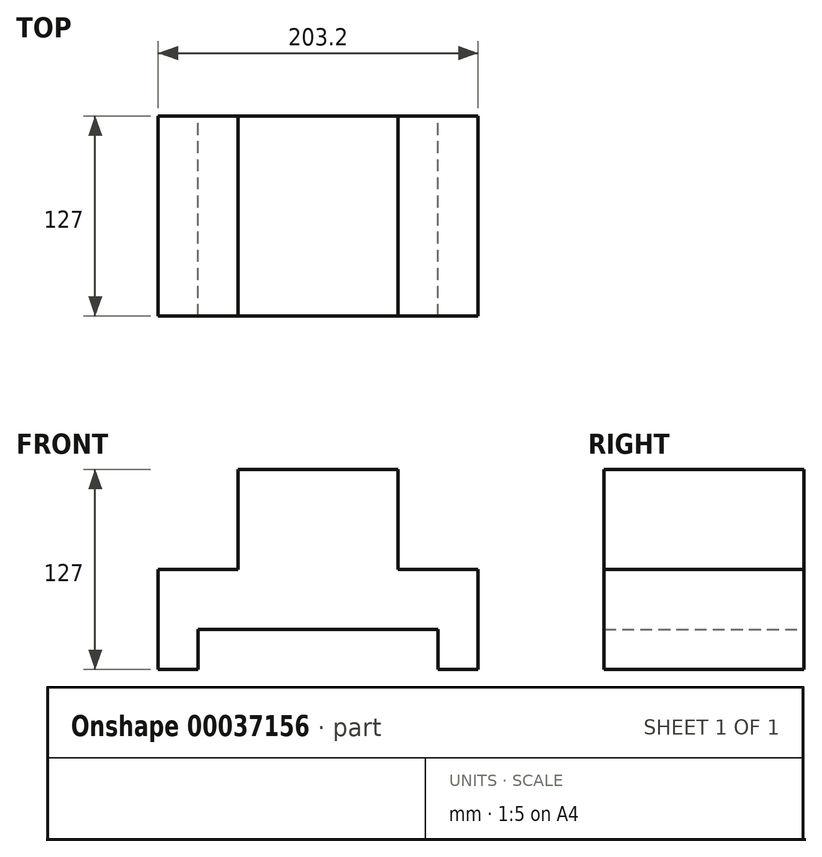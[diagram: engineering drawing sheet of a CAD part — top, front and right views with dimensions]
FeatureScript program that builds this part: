
annotation { "Feature Type Name" : "Feature", "Feature Type Description" : "" }
export const myFeature = defineFeature(function(context is Context, id is Id, definition is map)
    precondition{}
    {
        {
            var Q0;
            Q0=qCreatedBy(makeId("Front.planeOp"),FACE);
            var sketch = newSketch(context, id + "F0", { "sketchPlane" : qUnion([Q0])});
            skLineSegment(sketch, "E0", {"start": v(-101.3, -61.52) * mm, "end": v(-101.3, 1.98) * mm});
            skLineSegment(sketch, "E1", {"start": v(-101.3, 1.98) * mm, "end": v(-50.5, 1.98) * mm});
            skLineSegment(sketch, "E2", {"start": v(-50.5, 1.98) * mm, "end": v(-50.5, 65.48) * mm});
            skLineSegment(sketch, "E3", {"start": v(-50.5, 65.48) * mm, "end": v(51.1, 65.48) * mm});
            skLineSegment(sketch, "E4", {"start": v(51.1, 65.48) * mm, "end": v(51.1, 1.98) * mm});
            skLineSegment(sketch, "E5", {"start": v(51.1, 1.98) * mm, "end": v(101.9, 1.98) * mm});
            skLineSegment(sketch, "E6", {"start": v(101.9, 1.98) * mm, "end": v(101.9, -61.52) * mm});
            skLineSegment(sketch, "E7", {"start": v(101.9, -61.52) * mm, "end": v(76.5, -61.52) * mm});
            skLineSegment(sketch, "E8", {"start": v(76.5, -61.52) * mm, "end": v(76.5, -36.17) * mm});
            skLineSegment(sketch, "E9", {"start": v(76.5, -36.17) * mm, "end": v(-75.9, -36.17) * mm});
            skLineSegment(sketch, "E10", {"start": v(-75.9, -36.17) * mm, "end": v(-75.9, -61.52) * mm});
            skLineSegment(sketch, "E11", {"start": v(-75.9, -61.52) * mm, "end": v(-101.3, -61.52) * mm});
            skSolve(sketch);
        }
        {
            var Q0;
            Q0=makeQuery(id+"F0.imprint","IMPRINT",FACE,{"disambiguationData":[TD([[makeQuery(id+"F0.imprint","IMPRINT",EDGE,{"derivedFrom":sQuery(id+"F0.wireOp",EDGE,"E0")}),-1.0]])]});
            extrude(context, id + "F1", {"entities" : qUnion([Q0]), "depth" : 127 * mm});
        }
    });
